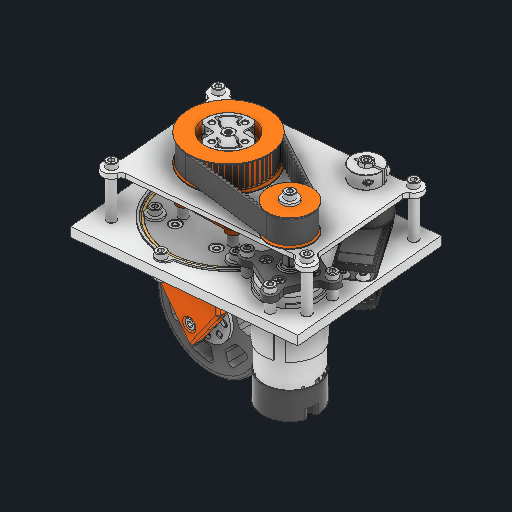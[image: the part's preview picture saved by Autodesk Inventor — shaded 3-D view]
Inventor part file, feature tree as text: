
AUTODESK INVENTOR PART (.ipt)
format: ipt  version: 2024.2 (Build 282272000, 272)  size: 62,754,816 bytes
history: native  units: in
note: dims shown in document units (in); Inventor stores cm internally (conversion verified against a paired STEP export)
features: other x3, plane x1
ambient origin geometry x8: Origin, YZ Plane, XZ Plane, XY Plane, X Axis, Y Axis, Z Axis, Center Point
bodies: Solid1 (feature_tree)
feature tree (4):
  other  "Pod_pre_mirror.ipt"
  other  "Solid1::Pod_pre_mirror.ipt"
  other  "TaggingFeature1"
  plane  "Work Plane2_1"
